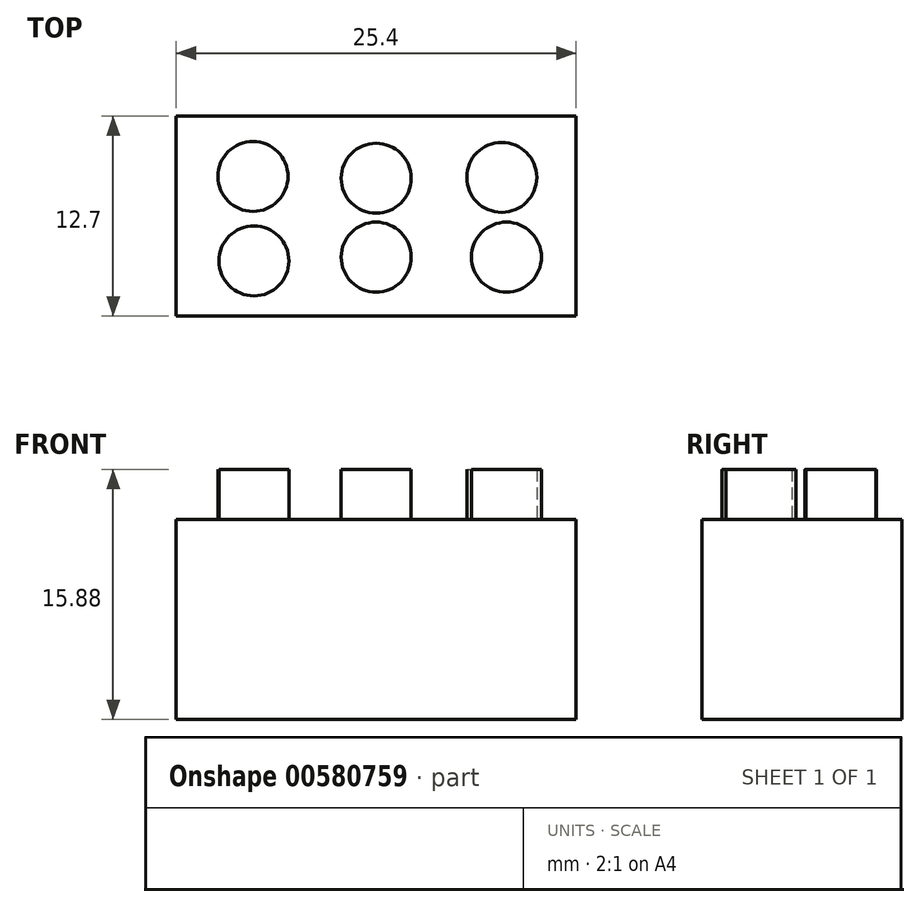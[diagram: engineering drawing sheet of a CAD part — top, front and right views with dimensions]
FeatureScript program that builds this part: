
annotation { "Feature Type Name" : "Feature", "Feature Type Description" : "" }
export const myFeature = defineFeature(function(context is Context, id is Id, definition is map)
    precondition{}
    {
        {
            var Q0;
            Q0=qCreatedBy(makeId("Front.planeOp"),FACE);
            var sketch = newSketch(context, id + "F0", { "sketchPlane" : qUnion([Q0])});
            skLineSegment(sketch, "E0.bottom", {"start": v(12.7, -6.35) * mm, "end": v(-12.7, -6.35) * mm});
            skLineSegment(sketch, "E0.top", {"start": v(12.7, 6.35) * mm, "end": v(-12.7, 6.35) * mm});
            skLineSegment(sketch, "E0.left", {"start": v(12.7, -6.35) * mm, "end": v(12.7, 6.35) * mm});
            skLineSegment(sketch, "E0.right", {"start": v(-12.7, -6.35) * mm, "end": v(-12.7, 6.35) * mm});
            skPoint(sketch, "E0.middle", {"position": v(0, 0) * mm});
            skSolve(sketch);
        }
        {
            var Q0;
            Q0 = qSketchRegion(id + "F0", true);
            extrude(context, id + "F1", {"entities" : qUnion([Q0]), "depth" : 12.7 * mm, "offsetDistance" : 25.4 * mm});
        }
        {
            var Q0;
            Q0=makeQuery(id+"F1.opExtrude","SWEPT_FACE",FACE,{"disambiguationData":[OSD([sQuery(id+"F0.wireOp",EDGE,"E0.top")])]});
            var sketch = newSketch(context, id + "F2", { "sketchPlane" : qUnion([Q0])});
            skCircle(sketch, "E1", {"center": v(0, -3.95) * mm, "radius": 2.22 * mm});
            skCircle(sketch, "E2", {"center": v(0, -8.96) * mm, "radius": 2.22 * mm});
            skCircle(sketch, "E3", {"center": v(8.27, -8.96) * mm, "radius": 2.22 * mm});
            skCircle(sketch, "E4", {"center": v(-7.76, -9.2) * mm, "radius": 2.22 * mm});
            skCircle(sketch, "E5", {"center": v(-7.82, -3.83) * mm, "radius": 2.22 * mm});
            skCircle(sketch, "E6", {"center": v(7.98, -3.9) * mm, "radius": 2.22 * mm});
            skSolve(sketch);
        }
        {
            var Q0;
            Q0=makeQuery(id+"F2.imprint","IMPRINT",FACE,{"disambiguationData":[TD([[makeQuery(id+"F2.imprint","IMPRINT",EDGE,{"derivedFrom":sQuery(id+"F2.wireOp",EDGE,"E4")}),1.0]])]});
            var Q1;
            Q1=makeQuery(id+"F2.imprint","IMPRINT",FACE,{"disambiguationData":[TD([[makeQuery(id+"F2.imprint","IMPRINT",EDGE,{"derivedFrom":sQuery(id+"F2.wireOp",EDGE,"E2")}),1.0]])]});
            var Q2;
            Q2=makeQuery(id+"F2.imprint","IMPRINT",FACE,{"disambiguationData":[TD([[makeQuery(id+"F2.imprint","IMPRINT",EDGE,{"derivedFrom":sQuery(id+"F2.wireOp",EDGE,"E3")}),1.0]])]});
            var Q3;
            Q3=makeQuery(id+"F2.imprint","IMPRINT",FACE,{"disambiguationData":[TD([[makeQuery(id+"F2.imprint","IMPRINT",EDGE,{"derivedFrom":sQuery(id+"F2.wireOp",EDGE,"E6")}),1.0]])]});
            var Q4;
            Q4=makeQuery(id+"F2.imprint","IMPRINT",FACE,{"disambiguationData":[TD([[makeQuery(id+"F2.imprint","IMPRINT",EDGE,{"derivedFrom":sQuery(id+"F2.wireOp",EDGE,"E1")}),1.0]])]});
            var Q5;
            Q5=makeQuery(id+"F2.imprint","IMPRINT",FACE,{"disambiguationData":[TD([[makeQuery(id+"F2.imprint","IMPRINT",EDGE,{"derivedFrom":sQuery(id+"F2.wireOp",EDGE,"E5")}),1.0]])]});
            extrude(context, id + "F3", {"entities" : qUnion([Q0, Q1, Q2, Q3, Q4, Q5]), "operationType" : NewBodyOperationType.ADD, "depth" : 3.17 * mm, "offsetDistance" : 25.4 * mm});
        }
    });
